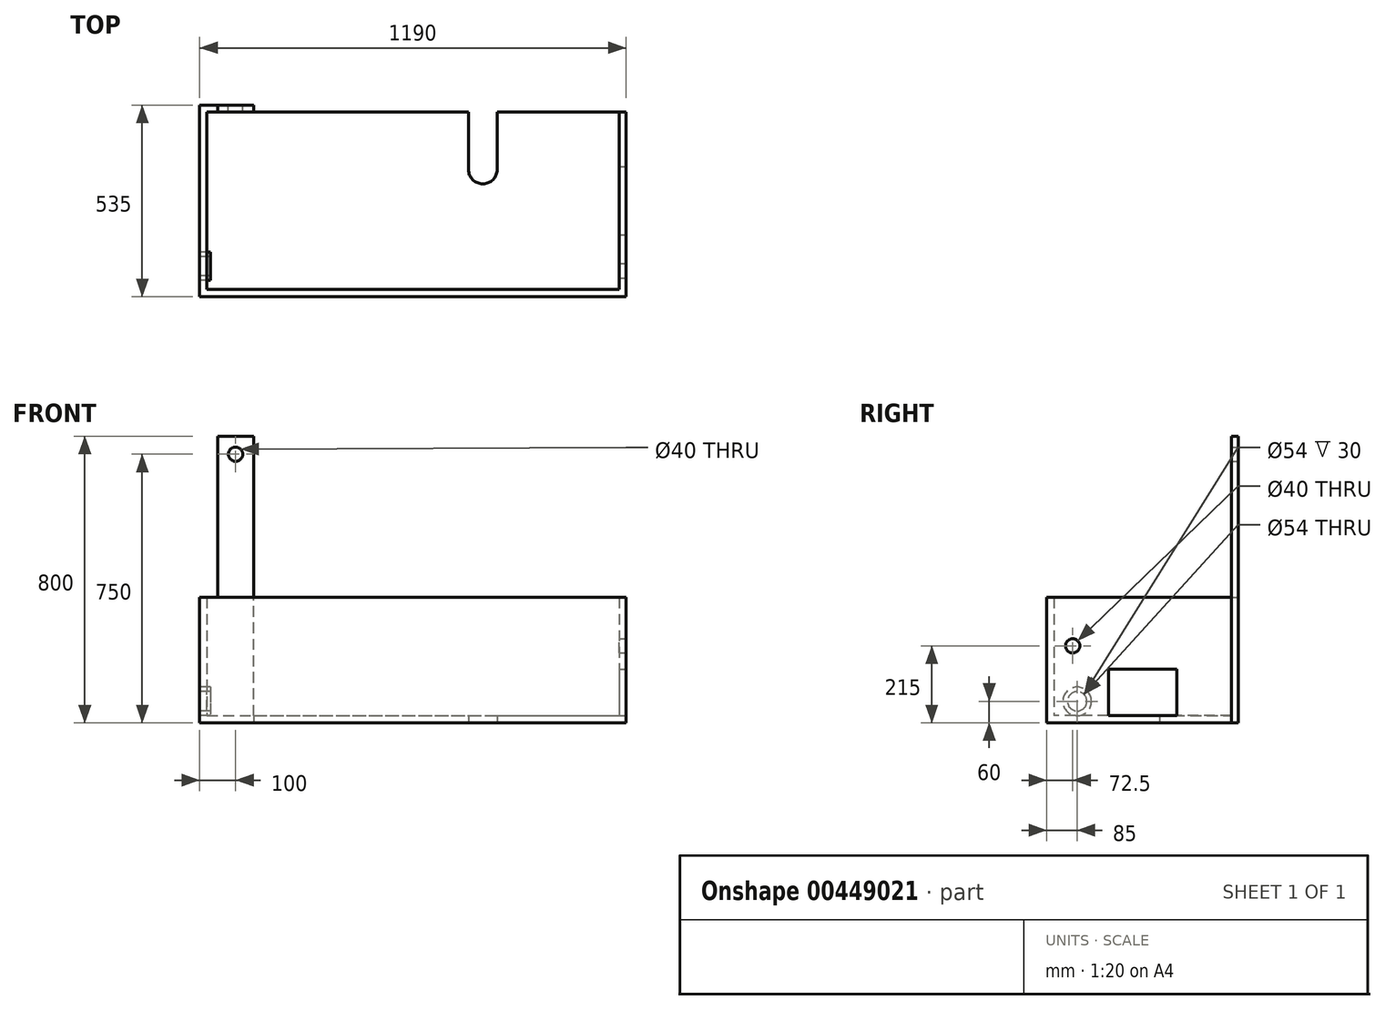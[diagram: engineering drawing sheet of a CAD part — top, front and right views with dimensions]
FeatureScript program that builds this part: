
annotation { "Feature Type Name" : "Feature", "Feature Type Description" : "" }
export const myFeature = defineFeature(function(context is Context, id is Id, definition is map)
    precondition{}
    {
        {
            var Q0;
            Q0=qCreatedBy(makeId("Top.planeOp"),FACE);
            var sketch = newSketch(context, id + "F0", { "sketchPlane" : qUnion([Q0])});
            skLineSegment(sketch, "E0.bottom", {"start": v(0, 0) * mm, "end": v(1190, 0) * mm});
            skLineSegment(sketch, "E0.top", {"start": v(0, 535) * mm, "end": v(1190, 535) * mm});
            skLineSegment(sketch, "E0.left", {"start": v(0, 0) * mm, "end": v(0, 535) * mm});
            skLineSegment(sketch, "E0.right", {"start": v(1190, 0) * mm, "end": v(1190, 535) * mm});
            skLineSegment(sketch, "E1.bottom", {"start": v(20, 515) * mm, "end": v(1170, 515) * mm});
            skLineSegment(sketch, "E1.top", {"start": v(20, 20) * mm, "end": v(1170, 20) * mm});
            skLineSegment(sketch, "E1.left", {"start": v(20, 515) * mm, "end": v(20, 20) * mm});
            skLineSegment(sketch, "E1.right", {"start": v(1170, 515) * mm, "end": v(1170, 20) * mm});
            skCircle(sketch, "E2", {"center": v(790, 355) * mm, "radius": 40 * mm});
            skLineSegment(sketch, "E3.bottom", {"start": v(750, 355) * mm, "end": v(830, 355) * mm});
            skLineSegment(sketch, "E3.top", {"start": v(750, 515) * mm, "end": v(830, 515) * mm});
            skLineSegment(sketch, "E3.left", {"start": v(750, 355) * mm, "end": v(750, 515) * mm});
            skLineSegment(sketch, "E3.right", {"start": v(830, 355) * mm, "end": v(830, 515) * mm});
            skSolve(sketch);
        }
        {
            var Q0;
            Q0=makeQuery(id+"F0.imprint","IMPRINT",FACE,{"disambiguationData":[TD([[makeQuery(id+"F0.imprint","IMPRINT",EDGE,{"derivedFrom":sQuery(id+"F0.wireOp",EDGE,"E0.bottom")}),1.0]])]});
            extrude(context, id + "F1", {"entities" : qUnion([Q0]), "depth" : 350 * mm});
        }
        {
            var Q0;
            Q0=makeQuery(id+"F0.imprint","IMPRINT",FACE,{"disambiguationData":[TD([[makeQuery(id+"F0.imprint","IMPRINT",EDGE,{"derivedFrom":sQuery(id+"F0.wireOp",EDGE,"E1.bottom")}),-1.0]])]});
            extrude(context, id + "F2", {"entities" : qUnion([Q0]), "operationType" : NewBodyOperationType.ADD, "depth" : 20 * mm});
        }
        {
            var Q0;
            Q0=makeQuery(id+"F1.opExtrude","SWEPT_FACE",FACE,{"disambiguationData":[OSD([sQuery(id+"F0.wireOp",EDGE,"E0.right")])]});
            var sketch = newSketch(context, id + "F3", { "sketchPlane" : qUnion([Q0])});
            skCircle(sketch, "E4", {"center": v(72.5, 215) * mm, "radius": 20 * mm});
            skLineSegment(sketch, "E5", {"start": v(72.5, 215) * mm, "end": v(0, 215) * mm, "construction": true});
            skLineSegment(sketch, "E6.bottom", {"start": v(172.5, 150) * mm, "end": v(362.5, 150) * mm});
            skLineSegment(sketch, "E6.top", {"start": v(172.5, 20) * mm, "end": v(362.5, 20) * mm});
            skLineSegment(sketch, "E6.left", {"start": v(172.5, 150) * mm, "end": v(172.5, 20) * mm});
            skLineSegment(sketch, "E6.right", {"start": v(362.5, 150) * mm, "end": v(362.5, 20) * mm});
            skSolve(sketch);
        }
        {
            var Q0;
            Q0=makeQuery(id+"F3.imprint","IMPRINT",FACE,{"disambiguationData":[TD([[makeQuery(id+"F3.imprint","IMPRINT",EDGE,{"derivedFrom":sQuery(id+"F3.wireOp",EDGE,"E4")}),1.0]])]});
            extrude(context, id + "F4", {"entities" : qUnion([Q0]), "operationType" : NewBodyOperationType.REMOVE, "oppositeDirection" : true, "depth" : 25 * mm});
        }
        {
            var Q0;
            Q0=makeQuery(id+"F1.opExtrude","SWEPT_FACE",FACE,{"disambiguationData":[OSD([sQuery(id+"F0.wireOp",EDGE,"E0.top")])]});
            var sketch = newSketch(context, id + "F5", { "sketchPlane" : qUnion([Q0])});
            skLineSegment(sketch, "E7.bottom", {"start": v(-50, 350) * mm, "end": v(-150, 350) * mm});
            skLineSegment(sketch, "E7.left", {"start": v(-50, 350) * mm, "end": v(-50, 800) * mm});
            skLineSegment(sketch, "E7.right", {"start": v(-150, 350) * mm, "end": v(-150, 800) * mm});
            skCircle(sketch, "E8", {"center": v(-100, 750) * mm, "radius": 20 * mm});
            skLineSegment(sketch, "E9", {"start": v(-150, 800) * mm, "end": v(-50, 800) * mm});
            skLineSegment(sketch, "E10", {"start": v(-100, 750) * mm, "end": v(-50, 750) * mm, "construction": true});
            skLineSegment(sketch, "E11", {"start": v(-150, 350) * mm, "end": v(-150, 0) * mm});
            skSolve(sketch);
        }
        {
            var Q0;
            Q0=makeQuery(id+"F5.imprint","IMPRINT",FACE,{"disambiguationData":[TD([[makeQuery(id+"F5.imprint","IMPRINT",EDGE,{"derivedFrom":sQuery(id+"F5.wireOp",EDGE,"E7.bottom")}),-1.0]])]});
            extrude(context, id + "F6", {"entities" : qUnion([Q0]), "operationType" : NewBodyOperationType.ADD, "oppositeDirection" : true, "depth" : 20 * mm});
        }
        {
            var Q0;
            Q0=makeQuery(id+"F1.opExtrude","SWEPT_FACE",FACE,{"disambiguationData":[OSD([sQuery(id+"F0.wireOp",EDGE,"E0.left")])]});
            var sketch = newSketch(context, id + "F7", { "sketchPlane" : qUnion([Q0])});
            skCircle(sketch, "E12", {"center": v(-85, 60) * mm, "radius": 27 * mm});
            skLineSegment(sketch, "E13", {"start": v(-535, 60) * mm, "end": v(-85, 60) * mm});
            skCircle(sketch, "E14", {"center": v(-85, 60) * mm, "radius": 40 * mm});
            skSolve(sketch);
        }
        {
            var Q0;
            Q0=makeQuery(id+"F7.imprint","IMPRINT",FACE,{"disambiguationData":[TD([[makeQuery(id+"F7.imprint","IMPRINT",EDGE,{"derivedFrom":sQuery(id+"F7.wireOp",EDGE,"E12")}),1.0]])]});
            extrude(context, id + "F8", {"entities" : qUnion([Q0]), "operationType" : NewBodyOperationType.REMOVE, "oppositeDirection" : true, "depth" : 50 * mm});
        }
        {
            var Q0;
            Q0=makeQuery(id+"F7.imprint","IMPRINT",FACE,{"disambiguationData":[TD([[makeQuery(id+"F7.imprint","IMPRINT",EDGE,{"derivedFrom":sQuery(id+"F7.wireOp",EDGE,"E12")}),-1.0]])]});
            extrude(context, id + "F9", {"entities" : qUnion([Q0]), "oppositeDirection" : true, "depth" : 30 * mm});
        }
        {
            var Q0;
            {var subQ0=sQuery(id+"F5.wireOp",EDGE,"E11");Q0=makeQuery(id+"F5.imprint","IMPRINT",FACE,{"disambiguationData":[TD([[makeQuery(id+"F5.imprint","IMPRINT",EDGE,{"derivedFrom":subQ0}),-1.0]])]});}
            extrude(context, id + "F10", {"entities" : qUnion([Q0]), "operationType" : NewBodyOperationType.REMOVE, "oppositeDirection" : true, "depth" : 20 * mm});
        }
        {
            var Q0;
            Q0=makeQuery(id+"F3.imprint","IMPRINT",FACE,{"disambiguationData":[TD([[makeQuery(id+"F3.imprint","IMPRINT",EDGE,{"derivedFrom":sQuery(id+"F3.wireOp",EDGE,"E6.bottom")}),-1.0]])]});
            extrude(context, id + "F11", {"entities" : qUnion([Q0]), "operationType" : NewBodyOperationType.REMOVE, "oppositeDirection" : true, "depth" : 20 * mm});
        }
    });
